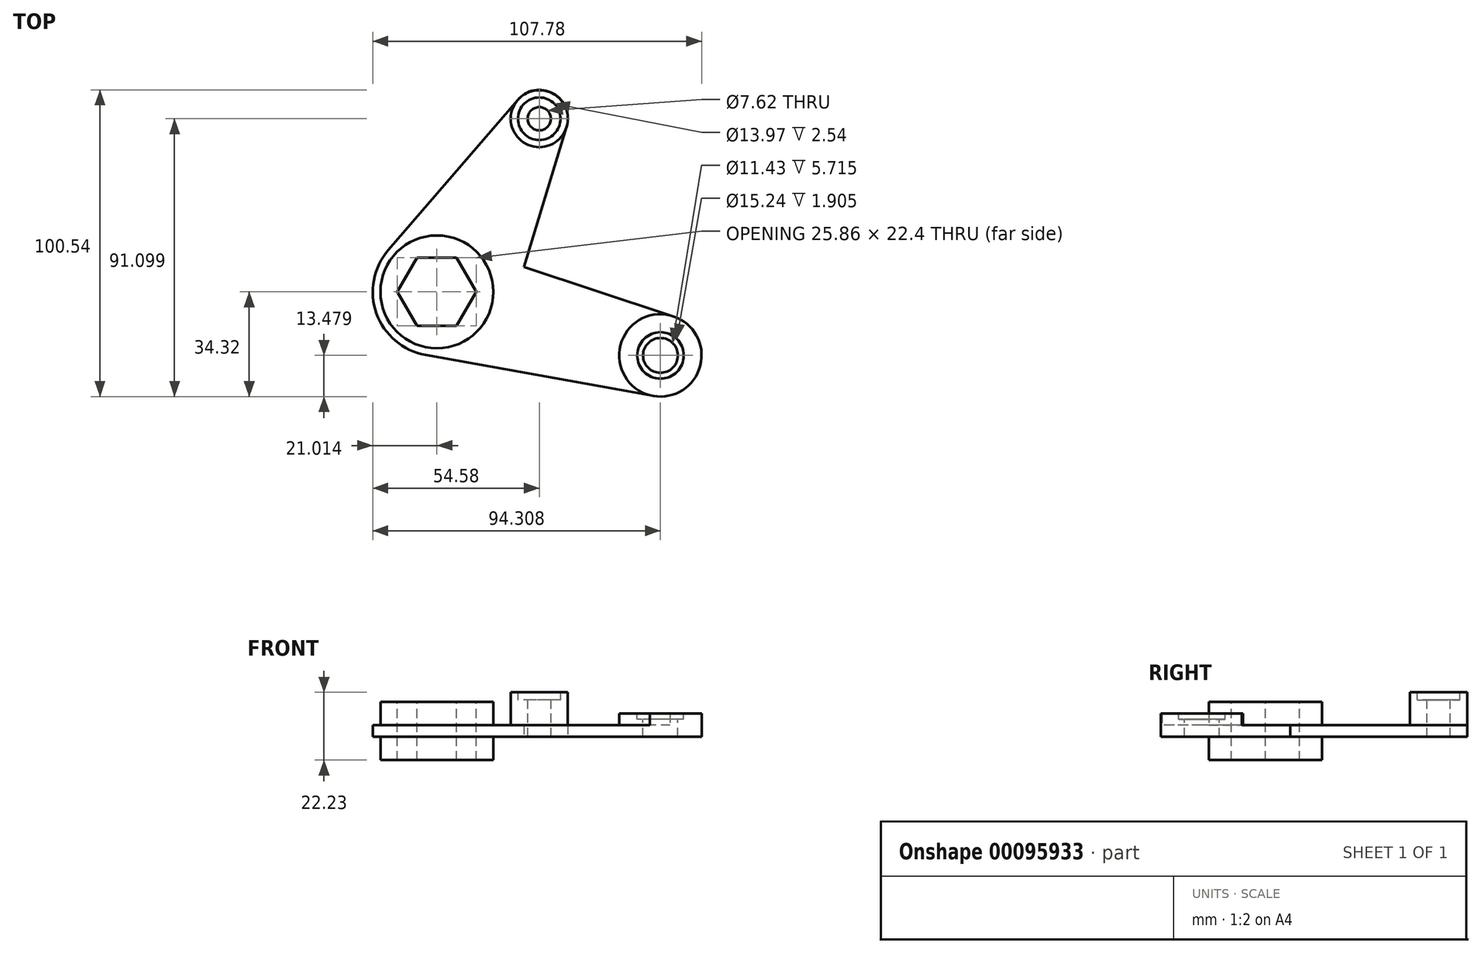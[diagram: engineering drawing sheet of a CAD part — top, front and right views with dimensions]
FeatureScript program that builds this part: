
annotation { "Feature Type Name" : "Feature", "Feature Type Description" : "" }
export const myFeature = defineFeature(function(context is Context, id is Id, definition is map)
    precondition{}
    {
        {
            var Q0;
            Q0=qCreatedBy(makeId("Top.planeOp"),FACE);
            var sketch = newSketch(context, id + "F0", { "sketchPlane" : qUnion([Q0])});
            skArc(sketch, "E0", {"start": v(-69.2, 13.7) * mm, "mid": v(-73.08, -7.03) * mm, "end": v(-57, -20.68) * mm});
            skArc(sketch, "E1", {"start": v(17.63, -34.1) * mm, "mid": v(33.08, -24.16) * mm, "end": v(24.25, -8.05) * mm});
            skLineSegment(sketch, "E2", {"start": v(-57, -20.68) * mm, "end": v(17.63, -34.1) * mm});
            skArc(sketch, "E3", {"start": v(-10.75, 54.1) * mm, "mid": v(-15.2, 65.06) * mm, "end": v(-26.83, 62.96) * mm});
            skLineSegment(sketch, "E4", {"start": v(-69.2, 13.7) * mm, "end": v(-26.83, 62.96) * mm});
            skLineSegment(sketch, "E5", {"start": v(24.25, -8.05) * mm, "end": v(-24.75, 8.18) * mm});
            skLineSegment(sketch, "E6", {"start": v(-24.75, 8.18) * mm, "end": v(-10.75, 54.1) * mm});
            skSolve(sketch);
        }
        {
            var Q0;
            Q0 = qSketchRegion(id + "F0", true);
            extrude(context, id + "F1", {"entities" : qUnion([Q0]), "endBound" : BoundingType.SYMMETRIC, "depth" : 3.8 * mm});
        }
        {
            var Q0;
            Q0=qCreatedBy(makeId("Top.planeOp"),FACE);
            var sketch = newSketch(context, id + "F2", { "sketchPlane" : qUnion([Q0])});
            skCircle(sketch, "E7", {"center": v(-19.71, 56.78) * mm, "radius": 9.34 * mm});
            skSolve(sketch);
        }
        {
            var Q0;
            Q0 = qSketchRegion(id + "F2", true);
            extrude(context, id + "F3", {"entities" : qUnion([Q0]), "operationType" : NewBodyOperationType.ADD, "depth" : 12.7 * mm});
        }
        {
            var Q0;
            Q0=makeQuery(id+"F1.opExtrude","CAP_FACE",FACE,{"disambiguationData":[OSD([sQuery(id+"F0.wireOp",EDGE,"E0"),sQuery(id+"F0.wireOp",EDGE,"E1"),sQuery(id+"F0.wireOp",EDGE,"E2"),sQuery(id+"F0.wireOp",EDGE,"E3"),sQuery(id+"F0.wireOp",EDGE,"E4"),sQuery(id+"F0.wireOp",EDGE,"E5"),sQuery(id+"F0.wireOp",EDGE,"E6")])],"isStart":false});
            var sketch = newSketch(context, id + "F4", { "sketchPlane" : qUnion([Q0])});
            skCircle(sketch, "E8", {"center": v(20.02, -20.84) * mm, "radius": 13.52 * mm});
            skSolve(sketch);
        }
        {
            var Q0;
            {var subQ5=makeQuery(id+"F1.opExtrude","CAP_EDGE",EDGE,{"disambiguationData":[OSD([sQuery(id+"F0.wireOp",EDGE,"E1")])],"isStart":false});Q0=makeQuery(id+"F4.imprint","IMPRINT",FACE,{"disambiguationData":[TD([[makeQuery(id+"F4.imprint","IMPRINT",EDGE,{"derivedFrom":subQ5}),1.0]])]});}
            extrude(context, id + "F5", {"entities" : qUnion([Q0]), "operationType" : NewBodyOperationType.ADD, "depth" : 3.8 * mm});
        }
        {
            var Q0;
            Q0=qCreatedBy(makeId("Top.planeOp"),FACE);
            var sketch = newSketch(context, id + "F6", { "sketchPlane" : qUnion([Q0])});
            skCircle(sketch, "E9", {"center": v(-53.28, 0) * mm, "radius": 18.5 * mm});
            skSolve(sketch);
        }
        {
            var Q0;
            Q0 = qSketchRegion(id + "F6", true);
            extrude(context, id + "F7", {"entities" : qUnion([Q0]), "operationType" : NewBodyOperationType.ADD, "endBound" : BoundingType.SYMMETRIC, "depth" : 19.05 * mm});
        }
        {
            var Q0;
            Q0=makeQuery(id+"F3.opExtrude","CAP_FACE",FACE,{"disambiguationData":[OSD([sQuery(id+"F2.wireOp",EDGE,"E7")])],"isStart":false});
            var sketch = newSketch(context, id + "F8", { "sketchPlane" : qUnion([Q0])});
            skPoint(sketch, "E10", {"position": v(-19.71, 56.78) * mm});
            skSolve(sketch);
        }
        {
            var Q0;
            Q0=sQuery(id+"F8.wireOp",VERTEX,"E10");
            var Q1;
            Q1=makeQuery(id+"F1.opExtrude","SWEPT_BODY",BODY,{"disambiguationData":[OSD([sQuery(id+"F0.wireOp",EDGE,"E0"),sQuery(id+"F0.wireOp",EDGE,"E1"),sQuery(id+"F0.wireOp",EDGE,"E2"),sQuery(id+"F0.wireOp",EDGE,"E3"),sQuery(id+"F0.wireOp",EDGE,"E4"),sQuery(id+"F0.wireOp",EDGE,"E5"),sQuery(id+"F0.wireOp",EDGE,"E6")])]});
            hole(context, id + "F9", {"style" : HoleStyle.C_BORE, "endStyle" : HoleEndStyle.BLIND, "holeDiameter" : 7.62 * mm, "cBoreDiameter" : 13.97 * mm, "cBoreDepth" : 2.54 * mm, "holeDepth" : 101.6 * mm, "locations" : qUnion([Q0]), "scope" : qUnion([Q1])});
        }
        {
            var Q0;
            Q0=makeQuery(id+"F5.opExtrude","CAP_FACE",FACE,{"disambiguationData":[OSD([sQuery(id+"F0.wireOp",EDGE,"E1"),sQuery(id+"F0.wireOp",EDGE,"E2"),sQuery(id+"F0.wireOp",EDGE,"E5"),sQuery(id+"F4.wireOp",EDGE,"E8")])],"isStart":false});
            var sketch = newSketch(context, id + "F10", { "sketchPlane" : qUnion([Q0])});
            skPoint(sketch, "E11", {"position": v(20.02, -20.84) * mm});
            skSolve(sketch);
        }
        {
            var Q0;
            Q0=sQuery(id+"F10.wireOp",VERTEX,"E11");
            var Q1;
            Q1=makeQuery(id+"F1.opExtrude","SWEPT_BODY",BODY,{"disambiguationData":[OSD([sQuery(id+"F0.wireOp",EDGE,"E0"),sQuery(id+"F0.wireOp",EDGE,"E1"),sQuery(id+"F0.wireOp",EDGE,"E2"),sQuery(id+"F0.wireOp",EDGE,"E3"),sQuery(id+"F0.wireOp",EDGE,"E4"),sQuery(id+"F0.wireOp",EDGE,"E5"),sQuery(id+"F0.wireOp",EDGE,"E6")])]});
            hole(context, id + "F11", {"style" : HoleStyle.C_BORE, "endStyle" : HoleEndStyle.BLIND, "holeDiameter" : 11.43 * mm, "cBoreDiameter" : 15.24 * mm, "cBoreDepth" : 1.9 * mm, "holeDepth" : 101.6 * mm, "locations" : qUnion([Q0]), "scope" : qUnion([Q1])});
        }
        {
            var Q0;
            Q0=makeQuery(id+"F7.opExtrude","CAP_FACE",FACE,{"disambiguationData":[OSD([sQuery(id+"F6.wireOp",EDGE,"E9")])],"isStart":false});
            var sketch = newSketch(context, id + "F12", { "sketchPlane" : qUnion([Q0])});
            skCircle(sketch, "E12.cCircle", {"center": v(-53.28, 0) * mm, "radius": 12.93 * mm, "construction": true});
            skLineSegment(sketch, "E12.0", {"start": v(-59.74, 11.2) * mm, "end": v(-46.81, 11.2) * mm});
            skLineSegment(sketch, "E12.1", {"start": v(-46.81, 11.2) * mm, "end": v(-40.35, 0) * mm});
            skLineSegment(sketch, "E12.2", {"start": v(-40.35, 0) * mm, "end": v(-46.81, -11.2) * mm});
            skLineSegment(sketch, "E12.3", {"start": v(-46.81, -11.2) * mm, "end": v(-59.74, -11.2) * mm});
            skLineSegment(sketch, "E12.4", {"start": v(-59.74, -11.2) * mm, "end": v(-66.2, 0) * mm});
            skLineSegment(sketch, "E12.5", {"start": v(-66.2, 0) * mm, "end": v(-59.74, 11.2) * mm});
            skSolve(sketch);
        }
        {
            var Q0;
            Q0=makeQuery(id+"F12.imprint","IMPRINT",FACE,{"disambiguationData":[TD([[makeQuery(id+"F12.imprint","IMPRINT",EDGE,{"derivedFrom":sQuery(id+"F12.wireOp",EDGE,"E12.0")}),-1.0]])]});
            extrude(context, id + "F13", {"entities" : qUnion([Q0]), "operationType" : NewBodyOperationType.REMOVE, "endBound" : BoundingType.THROUGH_ALL, "oppositeDirection" : true, "depth" : 25.4 * mm});
        }
    });
